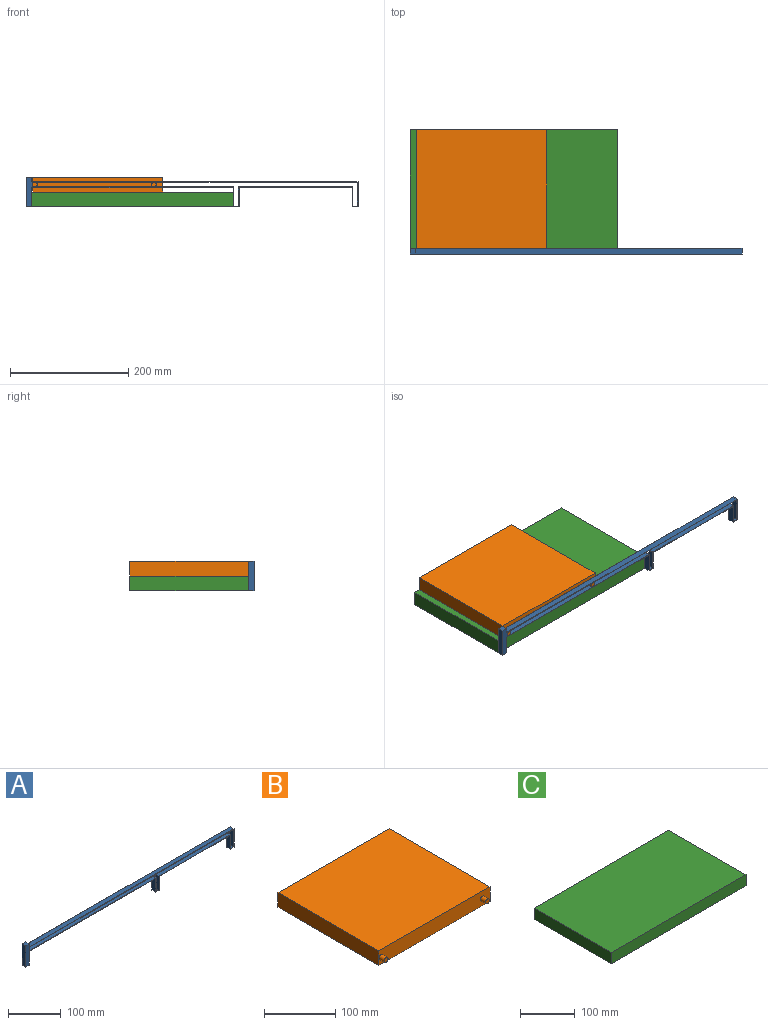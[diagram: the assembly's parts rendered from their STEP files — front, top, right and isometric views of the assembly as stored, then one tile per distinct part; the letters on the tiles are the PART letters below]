
ASSEMBLY  parts=3 mates=2
PART A: 26 faces, bbox 561x10x50 mm
  f0: plane 32.5x10mm, normal (1,0,0), area 325mm2, adj f1,f23,f24,f25
  f1: plane 340x10mm, normal (0,0,1), area 3400mm2, adj f0,f2,f24,f25
  f2: plane 10x8mm, normal (1,0,0), area 80mm2, adj f1,f3,f24,f25
  f3: plane 549x10mm, normal (0,0,-1), area 5490mm2, adj f2,f4,f24,f25
  f4: plane 40.5x10mm, normal (-1,0,0), area 405mm2, adj f3,f5,f24,f25
  f5: plane 10x8mm, normal (0,0,1), area 80mm2, adj f4,f6,f24,f25
  f6: plane 32.5x10mm, normal (1,0,0), area 325mm2, adj f5,f7,f24,f25
  f7: plane 193x10mm, normal (0,0,1), area 1930mm2, adj f6,f8,f24,f25
  f8: plane 32.5x10mm, normal (-1,0,0), area 325mm2, adj f7,f23,f24,f25
  f9: plane 340x10mm, normal (0,0,-1), area 3400mm2, adj f10,f22,f24,f25
  f10: plane 32.5x10mm, normal (-1,0,0), area 325mm2, adj f9,f11,f24,f25
  f11: plane 10x10mm, normal (0,0,-1), area 100mm2, adj f10,f12,f24,f25
  f12: plane 32.5x10mm, normal (1,0,0), area 325mm2, adj f11,f13,f24,f25
  f13: plane 191x10mm, normal (0,0,-1), area 1910mm2, adj f12,f14,f24,f25
  f14: plane 32.5x10mm, normal (-1,0,0), area 325mm2, adj f13,f15,f24,f25
  f15: plane 10x10mm, normal (0,0,-1), area 100mm2, adj f14,f16,f24,f25
  f16: plane 42.5x10mm, normal (1,0,0), area 425mm2, adj f15,f17,f24,f25
  f17: plane 551x10mm, normal (0,0,1), area 5510mm2, adj f16,f18,f24,f25
  f18: plane 10x7.5mm, normal (1,0,0), area 75mm2, adj f17,f19,f24,f25
  f19: plane 10x10mm, normal (0,0,1), area 100mm2, adj f18,f20,f24,f25
  f20: plane 50x10mm, normal (-1,0,0), area 500mm2, adj f19,f21,f24,f25
  f21: plane 10x10mm, normal (0,0,-1), area 100mm2, adj f20,f22,f24,f25
  f22: plane 32.5x10mm, normal (1,0,0), area 325mm2, adj f9,f21,f24,f25
  f23: plane 10x8mm, normal (0,0,1), area 80mm2, adj f0,f8,f24,f25
  f24: plane 561x50mm, normal (0,-1,0), area 1748mm2, adj f0,f1,f2,f3,f4,f5,f6,f7
  f25: plane 561x50mm, normal (0,1,0), area 1748mm2, adj f0,f1,f2,f3,f4,f5,f6,f7
PART B: 10 faces, bbox 220x210x25 mm
  f0: plane 200x25mm, normal (-1,0,0), area 5000mm2, adj f1,f3,f4,f5
  f1: plane 220x25mm, normal (0,-1,0), area 5399.5mm2, adj f0,f2,f4,f5,f6,f8
  f2: plane 200x25mm, normal (1,0,0), area 5000mm2, adj f1,f3,f4,f5
  f3: plane 220x25mm, normal (0,1,0), area 5500mm2, adj f0,f2,f4,f5
  f4: plane 220x200mm, normal (0,0,1), area 44000mm2, adj f0,f1,f2,f3
  f5: plane 220x200mm, normal (0,0,-1), area 44000mm2, adj f0,f1,f2,f3
  f6: cylinder r=4mm len=10mm, axis (0,1,0), area 251.3mm2, adj f1,f7
  f7: plane 8x8mm, normal (0,-1,0), area 50.3mm2, adj f6
  f8: cylinder r=4mm len=10mm, axis (0,1,0), area 251.3mm2, adj f1,f9
  f9: plane 8x8mm, normal (0,-1,0), area 50.3mm2, adj f8
PART C: 6 faces, bbox 350x200x25 mm
  f0: plane 350x25mm, normal (0,1,0), area 8750mm2, adj f1,f3,f4,f5
  f1: plane 200x25mm, normal (-1,0,0), area 5000mm2, adj f0,f2,f4,f5
  f2: plane 350x25mm, normal (0,-1,0), area 8750mm2, adj f1,f3,f4,f5
  f3: plane 200x25mm, normal (1,0,0), area 5000mm2, adj f0,f2,f4,f5
  f4: plane 350x200mm, normal (0,0,1), area 70000mm2, adj f0,f1,f2,f3
  f5: plane 350x200mm, normal (0,0,-1), area 70000mm2, adj f0,f1,f2,f3
PLACE A t=(-4,0,0)mm
PLACE B t=(-58,0,25)mm
PLACE C t=(-4,0,0)mm
MATE pin_slot B.f6 <-> A.f24  axis (0,-1,0) through (-164,-110,37.5)mm
MATE fastened A.f25 <-> C.f2  axis (0,1,0) through (-179,-100,0)mm
